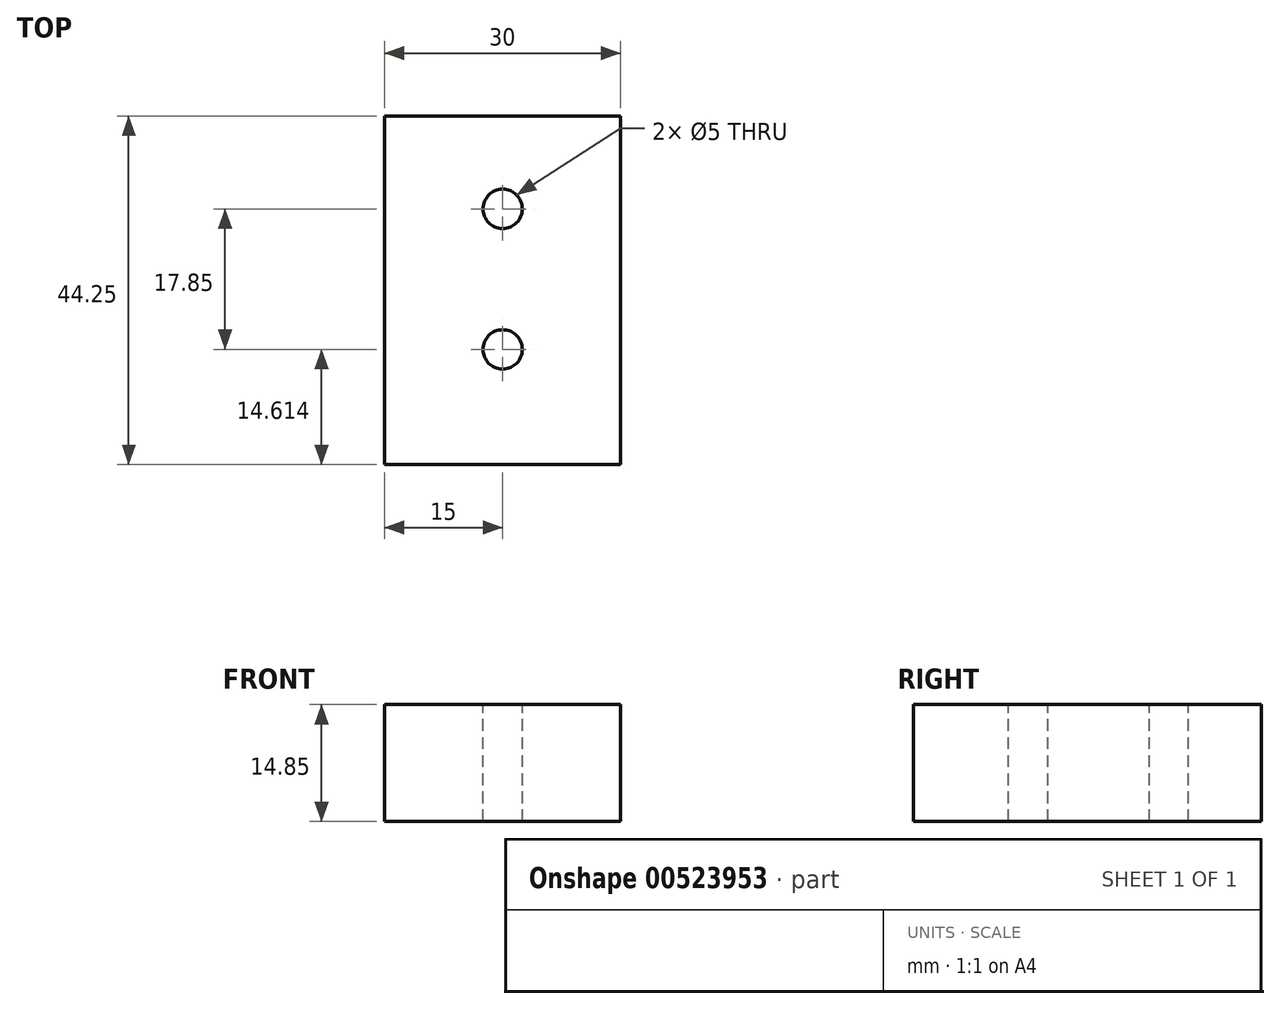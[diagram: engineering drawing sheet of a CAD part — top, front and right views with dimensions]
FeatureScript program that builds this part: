
annotation { "Feature Type Name" : "Feature", "Feature Type Description" : "" }
export const myFeature = defineFeature(function(context is Context, id is Id, definition is map)
    precondition{}
    {
        {
            var Q0;
            Q0=qCreatedBy(makeId("Front.planeOp"),FACE);
            var sketch = newSketch(context, id + "F0", { "sketchPlane" : qUnion([Q0])});
            skLineSegment(sketch, "E0.bottom", {"start": v(0, 0) * mm, "end": v(30, 0) * mm});
            skLineSegment(sketch, "E0.top", {"start": v(0, 14.85) * mm, "end": v(30, 14.85) * mm});
            skLineSegment(sketch, "E0.left", {"start": v(0, 0) * mm, "end": v(0, 14.85) * mm});
            skLineSegment(sketch, "E0.right", {"start": v(30, 0) * mm, "end": v(30, 14.85) * mm});
            skSolve(sketch);
        }
        {
            var Q0;
            Q0 = qSketchRegion(id + "F0", true);
            extrude(context, id + "F1", {"entities" : qUnion([Q0]), "depth" : 44.25 * mm, "offsetDistance" : 25 * mm});
        }
        {
            var Q0;
            Q0=makeQuery(id+"F1.opExtrude","SWEPT_FACE",FACE,{"disambiguationData":[OSD([sQuery(id+"F0.wireOp",EDGE,"E0.top")])]});
            var sketch = newSketch(context, id + "F2", { "sketchPlane" : qUnion([Q0])});
            skLineSegment(sketch, "E1", {"start": v(15, 0) * mm, "end": v(15, -44.25) * mm, "construction": true});
            skPoint(sketch, "E2", {"position": v(15, -29.64) * mm});
            skPoint(sketch, "E3", {"position": v(15, -11.79) * mm});
            skSolve(sketch);
        }
        {
            var Q0;
            Q0=sQuery(id+"F2.wireOp",VERTEX,"E3");
            var Q1;
            Q1=sQuery(id+"F2.wireOp",VERTEX,"E2");
            var Q2;
            Q2=makeQuery(id+"F1.opExtrude","SWEPT_BODY",BODY,{"disambiguationData":[OSD([sQuery(id+"F0.wireOp",EDGE,"E0.bottom"),sQuery(id+"F0.wireOp",EDGE,"E0.top"),sQuery(id+"F0.wireOp",EDGE,"E0.left"),sQuery(id+"F0.wireOp",EDGE,"E0.right")])]});
            hole(context, id + "F3", {"style" : HoleStyle.SIMPLE, "endStyle" : HoleEndStyle.THROUGH, "standardTappedOrClearance" : lookupTablePath({ "standard" : "ISO", "engagement" : "75%", "pitch" : "1 mm", "size" : "M6", "type" : "Tapped" }), "standardBlindInLast" : lookupTablePath({ "standard" : "ISO", "engagement" : "75%", "pitch" : "1 mm", "size" : "M6", "type" : "Tapped" }), "holeDiameter" : 5 * mm, "majorDiameter" : 6 * mm, "showTappedDepth" : true, "isTappedThrough" : true, "tappedDepth" : 12 * mm, "tapClearance" : 3, "locations" : qUnion([Q0, Q1]), "scope" : qUnion([Q2])});
        }
    });
